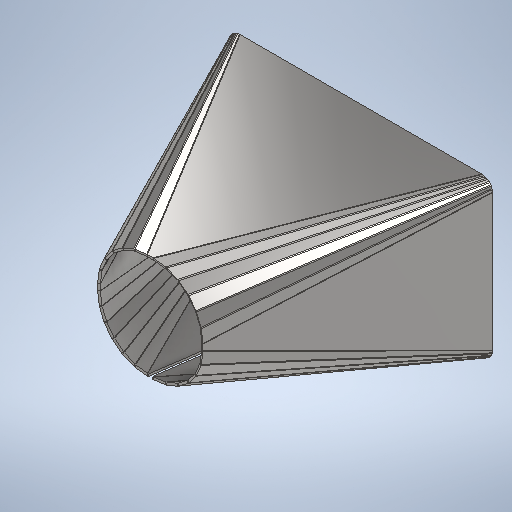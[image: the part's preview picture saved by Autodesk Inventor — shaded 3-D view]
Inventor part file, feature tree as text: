
AUTODESK INVENTOR PART (.ipt)
format: ipt  version: 2025.2 (Build 292293000, 293)  size: 428,032 bytes
history: native  units: mm
features: sketch x2, plane x1, loft x1, sheet_metal_op x1
ambient origin geometry x8: Origin, YZ Plane, XZ Plane, XY Plane, X Axis, Y Axis, Z Axis, Center Point
bodies: Solid1 (feature_tree)
feature tree (5):
  sketch  "Sketch1"  dims[d0=250.0mm d1=150.0mm]
  plane  "Work Plane1"
  loft  "Lofted Flange1"
  sketch  "Sketch2"  dims[d2=10.0mm d3=4.0mm d4=200.0mm d5=100.0mm d6=100.0mm d7=47.0mm d8=4.0mm d9=100.0mm d10=2.0mm d11=0.5mm d12=2.0mm d13=2.0mm d14=1.0mm d15=4.0mm d16=2.0mm]
  sheet_metal_op  "Bend1"
